# Revit family: E-917_RFA
name_source: partatom
category: Aparatos sanitarios
units: mm (PartAtom-declared; Revit-internal decimal feet)

## family parameters
Compartido = No
Corte con vacíos al cargar = No
Cota de conector redondo = Diámetro de uso
Número OmniClass = 23.45.00.00
Punto de cálculo de habitación = No
Se basa en plano de trabajo = No
Siempre vertical = Sí
Tipo de pieza = Normal
Título OmniClass = Sanitary, Laundry, and Cleaning Equipment

## types (1)
- E-917
    Accessories = Contra desagüe de push, Herramienta para sujeción, Llave para aireador, Llave para cartucho, Inserto para lavabo sin rebosadero, Mangueras Flexibles
    Brass Chromed = Brass
    Comentarios de tipo = Monomando de lavabo. Incluye contra de push. Incluye inserto para usarse con lavabos sin rebosadero. Compatible con lavabos de sobreponer (1 orificio), sobrecubierta o bajocubierta.
    Data Sheet = https://helvex.com.mx
    Descripción = Monomando para lavabo con desagüe de push y aireador oculto.
    Elevación por defecto = 0"
    Fabricante = HELVEX
    Installation Thread = ½" - 14 NPSM
    Instructive = https://helvex.com.mx
    Max. Working Pressure = 85.3 psi
    Min. Working Pressure = 5.7 psi
    Modelo = E-917
    Operation = El maneral tiene una rotación horizontal para la funciín de agua caliente y fría; y vertical para abrir y cerrar el flujo de agua.
    Support Base Diameter = 2"
    Total Depth = 8"
    Total Height = 7"
    URL = https://helvex.com.mx

## geometry (parser evidence)
native form markers: Sweep x2
no freeform markers — native parametric forms only
